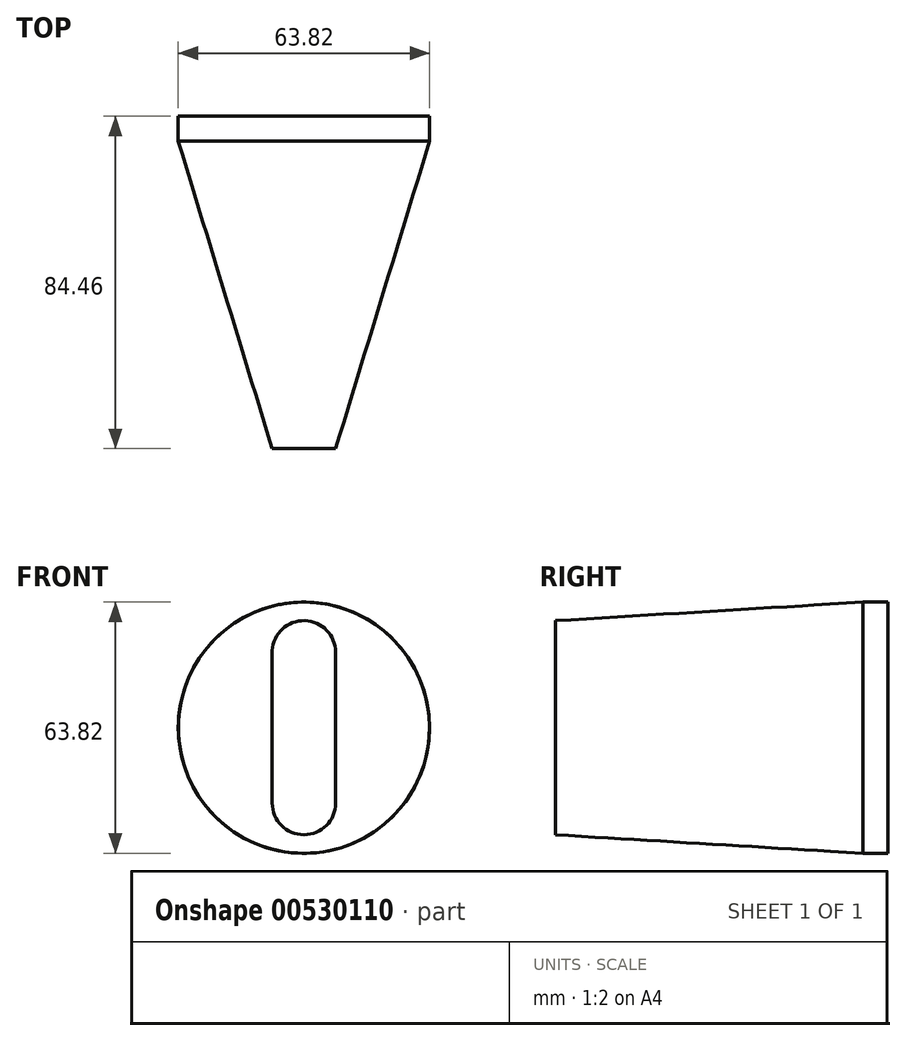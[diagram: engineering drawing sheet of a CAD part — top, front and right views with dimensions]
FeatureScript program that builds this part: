
annotation { "Feature Type Name" : "Feature", "Feature Type Description" : "" }
export const myFeature = defineFeature(function(context is Context, id is Id, definition is map)
    precondition{}
    {
        {
            var Q0;
            Q0=qCreatedBy(makeId("Front.planeOp"),FACE);
            var sketch = newSketch(context, id + "F0", { "sketchPlane" : qUnion([Q0])});
            skCircle(sketch, "E0", {"center": v(0, 0) * mm, "radius": 31.9 * mm});
            skSolve(sketch);
        }
        {
            var Q0;
            Q0=qCreatedBy(makeId("Front.planeOp"),FACE);
            cPlane(context, id + "F1", {"entities" : qUnion([Q0]), "cplaneType" : CPlaneType.OFFSET, "offset" : 81.28 * mm, "width" : 152.4 * mm, "height" : 152.4 * mm});
        }
        {
            var Q0;
            Q0=qCreatedBy(id+"F1.planeOp",FACE);
            var sketch = newSketch(context, id + "F2", { "sketchPlane" : qUnion([Q0])});
            skLineSegment(sketch, "E1.bottom", {"start": v(8.06, -19.14) * mm, "end": v(-8.06, -19.14) * mm, "construction": true});
            skLineSegment(sketch, "E1.top", {"start": v(8.06, 19.14) * mm, "end": v(-8.06, 19.14) * mm, "construction": true});
            skLineSegment(sketch, "E1.left", {"start": v(8.06, -19.14) * mm, "end": v(8.06, 19.14) * mm});
            skLineSegment(sketch, "E1.right", {"start": v(-8.06, -19.14) * mm, "end": v(-8.06, 19.14) * mm});
            skPoint(sketch, "E1.middle", {"position": v(0, 0) * mm});
            skArc(sketch, "E2", {"start": v(8.06, 19.14) * mm, "mid": v(0, 27.2) * mm, "end": v(-8.06, 19.14) * mm});
            skArc(sketch, "E3", {"start": v(-8.06, -19.14) * mm, "mid": v(0, -27.2) * mm, "end": v(8.06, -19.14) * mm});
            skSolve(sketch);
        }
        {
            var Q0;
            Q0=makeQuery(id+"F0.imprint","IMPRINT",FACE,{"disambiguationData":[TD([[makeQuery(id+"F0.imprint","IMPRINT",EDGE,{"derivedFrom":sQuery(id+"F0.wireOp",EDGE,"E0")}),1.0]])]});
            extrude(context, id + "F3", {"entities" : qUnion([Q0]), "endBound" : BoundingType.SYMMETRIC, "depth" : 6.35 * mm, "offsetDistance" : 25.4 * mm});
        }
        {
            var Q0;
            Q0=makeQuery(id+"F3.opExtrude","CAP_FACE",FACE,{"disambiguationData":[OSD([sQuery(id+"F0.wireOp",EDGE,"E0")])],"isStart":false});
            var sketch = newSketch(context, id + "F4", { "sketchPlane" : qUnion([Q0])});
            skArc(sketch, "E4", {"start": v(-7.9, 30.92) * mm, "mid": v(-31.9, 0.17) * mm, "end": v(-8.22, -30.83) * mm});
            skArc(sketch, "E5", {"start": v(8.88, 30.65) * mm, "mid": v(0.51, 31.9) * mm, "end": v(-7.9, 30.92) * mm});
            skArc(sketch, "E6", {"start": v(-8.22, -30.83) * mm, "mid": v(0.62, -31.9) * mm, "end": v(9.4, -30.5) * mm});
            skArc(sketch, "E7", {"start": v(9.4, -30.5) * mm, "mid": v(31.9, 0.27) * mm, "end": v(8.88, 30.65) * mm});
            skSolve(sketch);
        }
        {
            var Q0;
            Q0=makeQuery(id+"F2.imprint","IMPRINT",FACE,{"disambiguationData":[TD([[makeQuery(id+"F2.imprint","IMPRINT",EDGE,{"derivedFrom":sQuery(id+"F2.wireOp",EDGE,"E1.left")}),1.0]])]});
            var Q1;
            Q1=makeQuery(id+"F4.imprint","IMPRINT",FACE,{"disambiguationData":[TD([[makeQuery(id+"F4.imprint","IMPRINT",EDGE,{"derivedFrom":sQuery(id+"F4.wireOp",EDGE,"E4")}),1.0]])]});
            loft(context, id + "F5", {"sheetProfilesArray" : [{ "sheetProfileEntities" : qUnion([Q0]) }, { "sheetProfileEntities" : qUnion([Q1]) }]});
        }
    });
